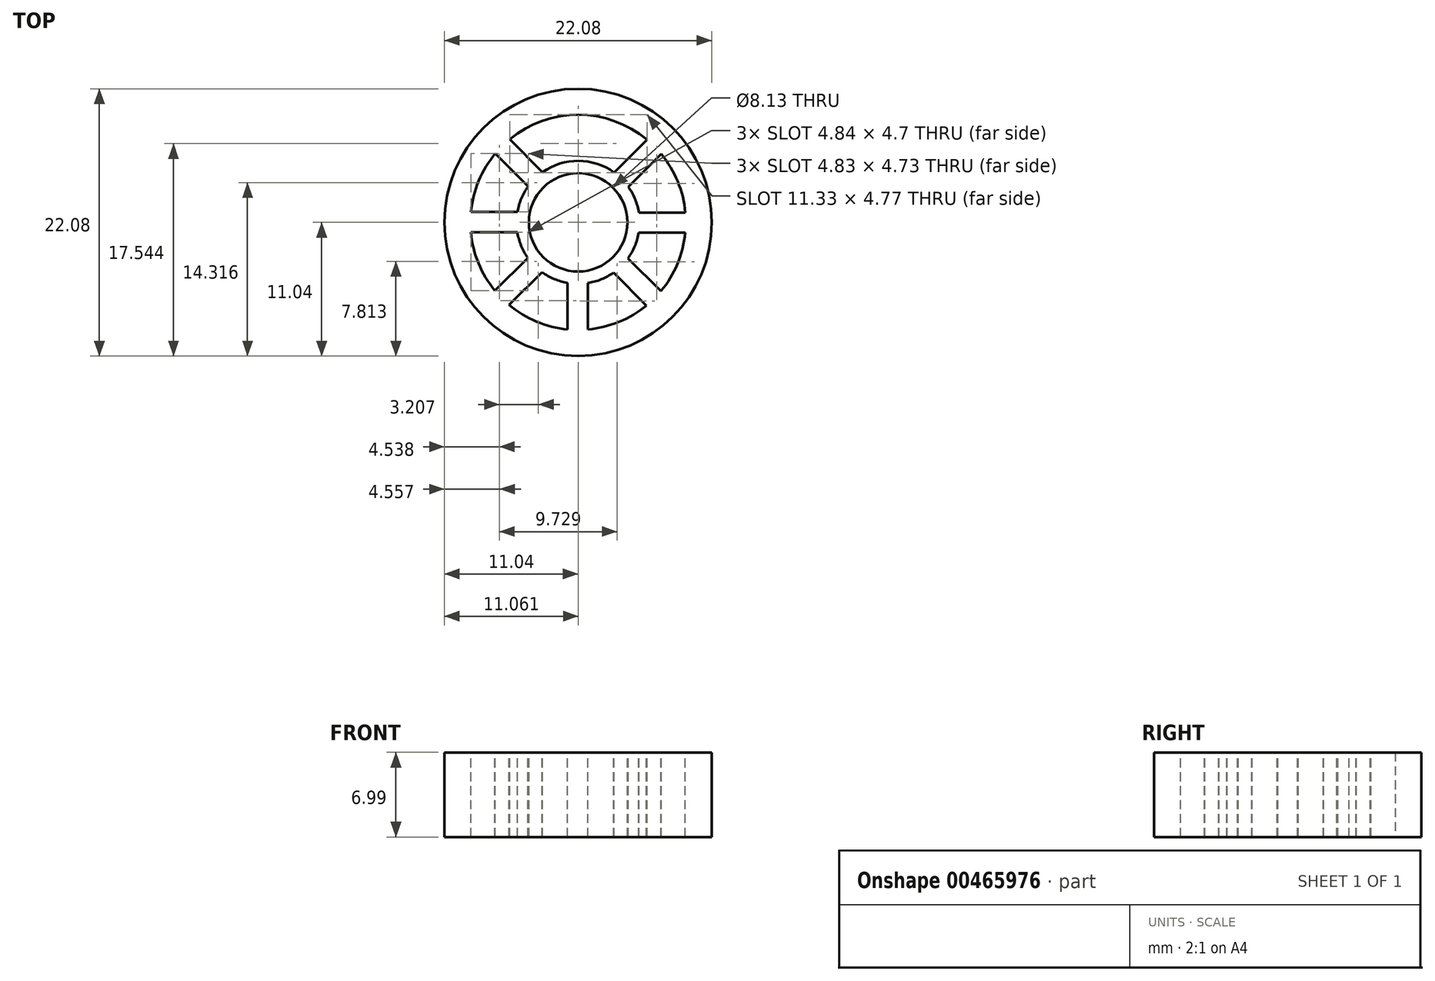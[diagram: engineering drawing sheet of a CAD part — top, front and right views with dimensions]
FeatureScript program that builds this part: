
annotation { "Feature Type Name" : "Feature", "Feature Type Description" : "" }
export const myFeature = defineFeature(function(context is Context, id is Id, definition is map)
    precondition{}
    {
        {
            var Q0;
            Q0=qCreatedBy(makeId("Top.planeOp"),FACE);
            var sketch = newSketch(context, id + "F0", { "sketchPlane" : qUnion([Q0])});
            skCircle(sketch, "E0", {"center": v(0, 0) * mm, "radius": 11.04 * mm});
            skCircle(sketch, "E1", {"center": v(0, 0) * mm, "radius": 8.9 * mm});
            skCircle(sketch, "E2", {"center": v(0, 0) * mm, "radius": 4.06 * mm});
            skCircle(sketch, "E3", {"center": v(0, 0) * mm, "radius": 5.08 * mm});
            skSolve(sketch);
        }
        {
            var Q0;
            Q0 = qSketchRegion(id + "F0", true);
            extrude(context, id + "F1", {"entities" : qUnion([Q0]), "depth" : 7 * mm});
        }
        {
            var Q0;
            Q0=makeQuery(id+"F1.opExtrude","CAP_FACE",FACE,{"disambiguationData":[OSD([sQuery(id+"F0.wireOp",EDGE,"E0"),sQuery(id+"F0.wireOp",EDGE,"E1")])],"isStart":false});
            var sketch = newSketch(context, id + "F2", { "sketchPlane" : qUnion([Q0])});
            skSolve(sketch);
        }
        {
            var Q0;
            Q0=makeQuery(id+"F2.imprint","IMPRINT",FACE,{"disambiguationData":[TD([[makeQuery(id+"F2.imprint","IMPRINT",EDGE,{"derivedFrom":makeQuery(id+"F1.opExtrude","CAP_EDGE",EDGE,{"disambiguationData":[OSD([sQuery(id+"F0.wireOp",EDGE,"E0")])],"isStart":false})}),1.0]])]});
            var sketch = newSketch(context, id + "F3", { "sketchPlane" : qUnion([Q0])});
            skCircle(sketch, "E4", {"center": v(0, 0) * mm, "radius": 4.06 * mm});
            skCircle(sketch, "E5", {"center": v(0, 0) * mm, "radius": 5.08 * mm});
            skSolve(sketch);
        }
        {
            var Q0;
            Q0=makeQuery(id+"F3.imprint","IMPRINT",FACE,{"disambiguationData":[TD([[makeQuery(id+"F3.imprint","IMPRINT",EDGE,{"derivedFrom":sQuery(id+"F3.wireOp",EDGE,"E4")}),-1.0]])]});
            extrude(context, id + "F4", {"entities" : qUnion([Q0]), "oppositeDirection" : true, "depth" : 7 * mm});
        }
        {
            var Q0;
            Q0=makeQuery(id+"F2.imprint","IMPRINT",FACE,{"disambiguationData":[TD([[makeQuery(id+"F2.imprint","IMPRINT",EDGE,{"derivedFrom":makeQuery(id+"F1.opExtrude","CAP_EDGE",EDGE,{"disambiguationData":[OSD([sQuery(id+"F0.wireOp",EDGE,"E0")])],"isStart":false})}),1.0]])]});
            var sketch = newSketch(context, id + "F5", { "sketchPlane" : qUnion([Q0])});
            skLineSegment(sketch, "E6", {"start": v(0, 4.59) * mm, "end": v(0, 9.25) * mm});
            skLineSegment(sketch, "E7", {"start": v(0, 9.25) * mm, "end": v(0.86, 9.25) * mm});
            skLineSegment(sketch, "E8", {"start": v(0.86, 9.25) * mm, "end": v(-0.8, 9.25) * mm});
            skPoint(sketch, "E8.endSnap0", {"position": v(0.43, 9.25) * mm});
            skLineSegment(sketch, "E9", {"start": v(-0.8, 9.25) * mm, "end": v(-0.8, 4.61) * mm});
            skLineSegment(sketch, "E10", {"start": v(-0.8, 4.61) * mm, "end": v(0, 4.59) * mm});
            skLineSegment(sketch, "E11", {"start": v(0.86, 4.59) * mm, "end": v(0.86, 9.25) * mm});
            skLineSegment(sketch, "E12", {"start": v(0, 4.59) * mm, "end": v(0.86, 4.59) * mm});
            skLineSegment(sketch, "E13.1.0", {"start": v(7.15, 5.93) * mm, "end": v(5.97, 7.11) * mm});
            skLineSegment(sketch, "E13.1.1", {"start": v(5.97, 7.11) * mm, "end": v(2.7, 3.83) * mm});
            skLineSegment(sketch, "E13.1.2", {"start": v(3.24, 3.24) * mm, "end": v(6.54, 6.54) * mm});
            skLineSegment(sketch, "E13.1.3", {"start": v(3.85, 2.63) * mm, "end": v(7.15, 5.93) * mm});
            skLineSegment(sketch, "E13.1.4", {"start": v(3.24, 3.24) * mm, "end": v(3.85, 2.63) * mm});
            skLineSegment(sketch, "E13.1.5", {"start": v(2.7, 3.83) * mm, "end": v(3.24, 3.24) * mm});
            skLineSegment(sketch, "E13.2.0", {"start": v(9.25, -0.86) * mm, "end": v(9.25, 0.8) * mm});
            skLineSegment(sketch, "E13.2.1", {"start": v(9.25, 0.8) * mm, "end": v(4.61, 0.8) * mm});
            skLineSegment(sketch, "E13.2.2", {"start": v(4.59, 0) * mm, "end": v(9.25, 0) * mm});
            skLineSegment(sketch, "E13.2.3", {"start": v(4.59, -0.86) * mm, "end": v(9.25, -0.86) * mm});
            skLineSegment(sketch, "E13.2.4", {"start": v(4.59, 0) * mm, "end": v(4.59, -0.86) * mm});
            skLineSegment(sketch, "E13.2.5", {"start": v(4.61, 0.8) * mm, "end": v(4.59, 0) * mm});
            skLineSegment(sketch, "E13.3.0", {"start": v(5.93, -7.15) * mm, "end": v(7.11, -5.97) * mm});
            skLineSegment(sketch, "E13.3.1", {"start": v(7.11, -5.97) * mm, "end": v(3.83, -2.7) * mm});
            skLineSegment(sketch, "E13.3.2", {"start": v(3.24, -3.24) * mm, "end": v(6.54, -6.54) * mm});
            skLineSegment(sketch, "E13.3.3", {"start": v(2.63, -3.85) * mm, "end": v(5.93, -7.15) * mm});
            skLineSegment(sketch, "E13.3.4", {"start": v(3.24, -3.24) * mm, "end": v(2.63, -3.85) * mm});
            skLineSegment(sketch, "E13.3.5", {"start": v(3.83, -2.7) * mm, "end": v(3.24, -3.24) * mm});
            skLineSegment(sketch, "E13.4.0", {"start": v(-0.86, -9.25) * mm, "end": v(0.8, -9.25) * mm});
            skLineSegment(sketch, "E13.4.1", {"start": v(0.8, -9.25) * mm, "end": v(0.8, -4.61) * mm});
            skLineSegment(sketch, "E13.4.2", {"start": v(0, -4.59) * mm, "end": v(0, -9.25) * mm});
            skLineSegment(sketch, "E13.4.3", {"start": v(-0.86, -4.59) * mm, "end": v(-0.86, -9.25) * mm});
            skLineSegment(sketch, "E13.4.4", {"start": v(0, -4.59) * mm, "end": v(-0.86, -4.59) * mm});
            skLineSegment(sketch, "E13.4.5", {"start": v(0.8, -4.61) * mm, "end": v(0, -4.59) * mm});
            skLineSegment(sketch, "E13.5.0", {"start": v(-7.15, -5.93) * mm, "end": v(-5.97, -7.11) * mm});
            skLineSegment(sketch, "E13.5.1", {"start": v(-5.97, -7.11) * mm, "end": v(-2.7, -3.83) * mm});
            skLineSegment(sketch, "E13.5.2", {"start": v(-3.24, -3.24) * mm, "end": v(-6.54, -6.54) * mm});
            skLineSegment(sketch, "E13.5.3", {"start": v(-3.85, -2.63) * mm, "end": v(-7.15, -5.93) * mm});
            skLineSegment(sketch, "E13.5.4", {"start": v(-3.24, -3.24) * mm, "end": v(-3.85, -2.63) * mm});
            skLineSegment(sketch, "E13.5.5", {"start": v(-2.7, -3.83) * mm, "end": v(-3.24, -3.24) * mm});
            skLineSegment(sketch, "E13.6.0", {"start": v(-9.25, 0.86) * mm, "end": v(-9.25, -0.8) * mm});
            skLineSegment(sketch, "E13.6.1", {"start": v(-9.25, -0.8) * mm, "end": v(-4.61, -0.8) * mm});
            skLineSegment(sketch, "E13.6.2", {"start": v(-4.59, 0) * mm, "end": v(-9.25, 0) * mm});
            skLineSegment(sketch, "E13.6.3", {"start": v(-4.59, 0.86) * mm, "end": v(-9.25, 0.86) * mm});
            skLineSegment(sketch, "E13.6.4", {"start": v(-4.59, 0) * mm, "end": v(-4.59, 0.86) * mm});
            skLineSegment(sketch, "E13.6.5", {"start": v(-4.61, -0.8) * mm, "end": v(-4.59, 0) * mm});
            skLineSegment(sketch, "E13.7.0", {"start": v(-5.93, 7.15) * mm, "end": v(-7.11, 5.97) * mm});
            skLineSegment(sketch, "E13.7.1", {"start": v(-7.11, 5.97) * mm, "end": v(-3.83, 2.7) * mm});
            skLineSegment(sketch, "E13.7.2", {"start": v(-3.24, 3.24) * mm, "end": v(-6.54, 6.54) * mm});
            skLineSegment(sketch, "E13.7.3", {"start": v(-2.63, 3.85) * mm, "end": v(-5.93, 7.15) * mm});
            skLineSegment(sketch, "E13.7.4", {"start": v(-3.24, 3.24) * mm, "end": v(-2.63, 3.85) * mm});
            skLineSegment(sketch, "E13.7.5", {"start": v(-3.83, 2.7) * mm, "end": v(-3.24, 3.24) * mm});
            skPoint(sketch, "E13.center", {"position": v(0, 0) * mm});
            skLineSegment(sketch, "E13.anchor1", {"start": v(0, 0) * mm, "end": v(-0.8, 9.25) * mm, "construction": true});
            skLineSegment(sketch, "E13.anchor2", {"start": v(0, 0) * mm, "end": v(-0.8, 9.25) * mm, "construction": true});
            skSolve(sketch);
        }
        {
            var Q0;
            {var subQ0=sQuery(id+"F5.wireOp",EDGE,"E12");Q0=makeQuery(id+"F5.imprint","IMPRINT",FACE,{"disambiguationData":[TD([[makeQuery(id+"F5.imprint","IMPRINT",EDGE,{"derivedFrom":subQ0}),1.0]])]});}
            var Q1;
            {var subQ0=sQuery(id+"F5.wireOp",EDGE,"E10");Q1=makeQuery(id+"F5.imprint","IMPRINT",FACE,{"disambiguationData":[TD([[makeQuery(id+"F5.imprint","IMPRINT",EDGE,{"derivedFrom":subQ0}),1.0]])]});}
            var Q2;
            {var subQ0=sQuery(id+"F5.wireOp",EDGE,"E13.7.5");Q2=makeQuery(id+"F5.imprint","IMPRINT",FACE,{"disambiguationData":[TD([[makeQuery(id+"F5.imprint","IMPRINT",EDGE,{"derivedFrom":subQ0}),1.0]])]});}
            var Q3;
            {var subQ0=sQuery(id+"F5.wireOp",EDGE,"E13.6.4");Q3=makeQuery(id+"F5.imprint","IMPRINT",FACE,{"disambiguationData":[TD([[makeQuery(id+"F5.imprint","IMPRINT",EDGE,{"derivedFrom":subQ0}),1.0]])]});}
            var Q4;
            {var subQ0=sQuery(id+"F5.wireOp",EDGE,"E13.6.5");Q4=makeQuery(id+"F5.imprint","IMPRINT",FACE,{"disambiguationData":[TD([[makeQuery(id+"F5.imprint","IMPRINT",EDGE,{"derivedFrom":subQ0}),1.0]])]});}
            var Q5;
            {var subQ0=sQuery(id+"F5.wireOp",EDGE,"E13.5.4");Q5=makeQuery(id+"F5.imprint","IMPRINT",FACE,{"disambiguationData":[TD([[makeQuery(id+"F5.imprint","IMPRINT",EDGE,{"derivedFrom":subQ0}),1.0]])]});}
            var Q6;
            {var subQ0=sQuery(id+"F5.wireOp",EDGE,"E13.5.5");Q6=makeQuery(id+"F5.imprint","IMPRINT",FACE,{"disambiguationData":[TD([[makeQuery(id+"F5.imprint","IMPRINT",EDGE,{"derivedFrom":subQ0}),1.0]])]});}
            var Q7;
            {var subQ0=sQuery(id+"F5.wireOp",EDGE,"E13.4.4");Q7=makeQuery(id+"F5.imprint","IMPRINT",FACE,{"disambiguationData":[TD([[makeQuery(id+"F5.imprint","IMPRINT",EDGE,{"derivedFrom":subQ0}),1.0]])]});}
            var Q8;
            {var subQ0=sQuery(id+"F5.wireOp",EDGE,"E13.4.5");Q8=makeQuery(id+"F5.imprint","IMPRINT",FACE,{"disambiguationData":[TD([[makeQuery(id+"F5.imprint","IMPRINT",EDGE,{"derivedFrom":subQ0}),1.0]])]});}
            var Q9;
            {var subQ0=sQuery(id+"F5.wireOp",EDGE,"E13.3.4");Q9=makeQuery(id+"F5.imprint","IMPRINT",FACE,{"disambiguationData":[TD([[makeQuery(id+"F5.imprint","IMPRINT",EDGE,{"derivedFrom":subQ0}),1.0]])]});}
            var Q10;
            {var subQ0=sQuery(id+"F5.wireOp",EDGE,"E13.3.5");Q10=makeQuery(id+"F5.imprint","IMPRINT",FACE,{"disambiguationData":[TD([[makeQuery(id+"F5.imprint","IMPRINT",EDGE,{"derivedFrom":subQ0}),1.0]])]});}
            var Q11;
            {var subQ0=sQuery(id+"F5.wireOp",EDGE,"E13.2.4");Q11=makeQuery(id+"F5.imprint","IMPRINT",FACE,{"disambiguationData":[TD([[makeQuery(id+"F5.imprint","IMPRINT",EDGE,{"derivedFrom":subQ0}),1.0]])]});}
            var Q12;
            {var subQ0=sQuery(id+"F5.wireOp",EDGE,"E13.2.5");Q12=makeQuery(id+"F5.imprint","IMPRINT",FACE,{"disambiguationData":[TD([[makeQuery(id+"F5.imprint","IMPRINT",EDGE,{"derivedFrom":subQ0}),1.0]])]});}
            var Q13;
            {var subQ0=sQuery(id+"F5.wireOp",EDGE,"E13.1.4");Q13=makeQuery(id+"F5.imprint","IMPRINT",FACE,{"disambiguationData":[TD([[makeQuery(id+"F5.imprint","IMPRINT",EDGE,{"derivedFrom":subQ0}),1.0]])]});}
            var Q14;
            {var subQ0=sQuery(id+"F5.wireOp",EDGE,"E13.1.5");Q14=makeQuery(id+"F5.imprint","IMPRINT",FACE,{"disambiguationData":[TD([[makeQuery(id+"F5.imprint","IMPRINT",EDGE,{"derivedFrom":subQ0}),1.0]])]});}
            var Q15;
            {var subQ0=sQuery(id+"F5.wireOp",EDGE,"E13.7.4");Q15=makeQuery(id+"F5.imprint","IMPRINT",FACE,{"disambiguationData":[TD([[makeQuery(id+"F5.imprint","IMPRINT",EDGE,{"derivedFrom":subQ0}),1.0]])]});}
            extrude(context, id + "F6", {"entities" : qUnion([Q0, Q1, Q2, Q3, Q4, Q5, Q6, Q7, Q8, Q9, Q10, Q11, Q12, Q13, Q14, Q15]), "operationType" : NewBodyOperationType.ADD, "oppositeDirection" : true, "depth" : 7 * mm});
        }
    });
